FCSTD DOCUMENT  (FreeCAD 0.21R33771 (Git))
Label: Model_2
License: All rights reserved
LicenseURL: http://en.wikipedia.org/wiki/All_rights_reserved
objects: Sketcher::SketchObject×2, App::FeaturePython×2, Spreadsheet::Sheet×1, App::DocumentObjectGroupPython×1
note: 2 computed .brp shape members not serialized (recipe doc carries the construction recipe); baked Part::Feature solids carry a one-line shape summary decoded from their .brp

FEATURE [Spreadsheet::Sheet] Spreadsheet  label="Parametry"
  cells = A1='Parametry palca pacjenta, wartości proszę wpisywać w milimetrach; A3='Proszę wrowadzić średnicę palca pacjenta; B3='Średnica palca; C3(Srednica)=20; A4='Proszę wprowadzić długość palca pacjenta; B4='Długość palca; C4(Dlugosc)=80
FEATURE [Sketcher::SketchObject] Sketch  label="Model_cięcia"
  FullyConstrained = true
  expr: Constraints[100] = <<Parametry>>.Srednica / 2
  expr: Constraints[101] = <<Parametry>>.Srednica / 2
  expr: Constraints[102] = <<Parametry>>.Srednica / 2
  expr: Constraints[137] = <<Parametry>>.Dlugosc + 10
  expr: Constraints[15] = <<Parametry>>.Srednica / 2
  expr: Constraints[16] = <<Parametry>>.Srednica / 2
  expr: Constraints[17] = <<Parametry>>.Srednica / 2
  expr: Constraints[18] = <<Parametry>>.Srednica / 2
  expr: Constraints[19] = <<Parametry>>.Srednica / 2
  expr: Constraints[20] = <<Parametry>>.Srednica / 2
  expr: Constraints[21] = <<Parametry>>.Srednica / 2
  expr: Constraints[22] = <<Parametry>>.Srednica / 2
  expr: Constraints[31] = <<Parametry>>.Srednica / 2
  expr: Constraints[32] = <<Parametry>>.Srednica / 2
  expr: Constraints[33] = <<Parametry>>.Srednica / 2
  expr: Constraints[34] = <<Parametry>>.Srednica / 2
  expr: Constraints[35] = <<Parametry>>.Srednica / 2
  expr: Constraints[36] = <<Parametry>>.Srednica / 2
  expr: Constraints[37] = <<Parametry>>.Srednica / 2
  expr: Constraints[38] = <<Parametry>>.Srednica / 2
  expr: Constraints[79] = <<Parametry>>.Srednica / 2
  expr: Constraints[80] = <<Parametry>>.Srednica / 2
  expr: Constraints[81] = <<Parametry>>.Srednica / 2
  expr: Constraints[82] = <<Parametry>>.Srednica / 2
  expr: Constraints[83] = <<Parametry>>.Srednica / 2
  expr: Constraints[84] = <<Parametry>>.Srednica / 2
  expr: Constraints[85] = <<Parametry>>.Srednica / 2
  expr: Constraints[86] = <<Parametry>>.Srednica / 2
  expr: Constraints[95] = <<Parametry>>.Srednica / 2
  expr: Constraints[96] = <<Parametry>>.Srednica / 2
  expr: Constraints[97] = <<Parametry>>.Srednica / 2
  expr: Constraints[98] = <<Parametry>>.Srednica / 2
  expr: Constraints[99] = <<Parametry>>.Srednica / 2
  sketch-geometry (56):
    g0: LineSegment StartX=0 StartY=0 StartZ=0 EndX=90 EndY=0 EndZ=0
    g1: LineSegment StartX=90 StartY=0 StartZ=0 EndX=90 EndY=60 EndZ=0
    g2: LineSegment StartX=90 StartY=60 StartZ=0 EndX=0 EndY=60 EndZ=0
    g3: LineSegment StartX=0 StartY=60 StartZ=0 EndX=0 EndY=0 EndZ=0
    g4: GeomPoint X=15 Y=15 Z=0
    g5: LineSegment StartX=15 StartY=5 StartZ=0 EndX=15 EndY=25 EndZ=0
    g6: LineSegment StartX=5 StartY=15 StartZ=0 EndX=25 EndY=15 EndZ=0
    g7: LineSegment StartX=7.92893 StartY=22.0711 StartZ=0 EndX=22.0711 EndY=7.92893 EndZ=0
    g8: LineSegment StartX=7.92893 StartY=7.92893 StartZ=0 EndX=22.0711 EndY=22.0711 EndZ=0
    g9: GeomPoint X=15 Y=45 Z=0
    g10: LineSegment StartX=15 StartY=35 StartZ=0 EndX=15 EndY=55 EndZ=0
    g11: LineSegment StartX=5 StartY=45 StartZ=0 EndX=25 EndY=45 EndZ=0
    g12: LineSegment StartX=7.92893 StartY=52.0711 StartZ=0 EndX=22.0711 EndY=37.9289 EndZ=0
    g13: LineSegment StartX=7.92893 StartY=37.9289 StartZ=0 EndX=22.0711 EndY=52.0711 EndZ=0
    g14: Circle CenterX=7.92893 CenterY=52.0711 CenterZ=0 NormalX=0 NormalY=0 NormalZ=1 AngleXU=0 Radius=0.25
    g15: Circle CenterX=15 CenterY=55 CenterZ=0 NormalX=0 NormalY=0 NormalZ=1 AngleXU=0 Radius=0.25
    g16: Circle CenterX=22.0711 CenterY=52.0711 CenterZ=0 NormalX=0 NormalY=0 NormalZ=1 AngleXU=0 Radius=0.25
    g17: Circle CenterX=25 CenterY=45 CenterZ=0 NormalX=0 NormalY=0 NormalZ=1 AngleXU=0 Radius=0.25
    g18: Circle CenterX=22.0711 CenterY=37.9289 CenterZ=0 NormalX=0 NormalY=0 NormalZ=1 AngleXU=0 Radius=0.25
    g19: Circle CenterX=15 CenterY=35 CenterZ=0 NormalX=0 NormalY=0 NormalZ=1 AngleXU=0 Radius=0.25
    g20: Circle CenterX=7.92893 CenterY=37.9289 CenterZ=0 NormalX=0 NormalY=0 NormalZ=1 AngleXU=0 Radius=0.25
    g21: Circle CenterX=5 CenterY=45 CenterZ=0 NormalX=0 NormalY=0 NormalZ=1 AngleXU=0 Radius=0.25
    g22: Circle CenterX=5 CenterY=15 CenterZ=0 NormalX=0 NormalY=0 NormalZ=1 AngleXU=0 Radius=0.25
    g23: Circle CenterX=7.92893 CenterY=22.0711 CenterZ=0 NormalX=0 NormalY=0 NormalZ=1 AngleXU=0 Radius=0.25
    g24: Circle CenterX=15 CenterY=25 CenterZ=0 NormalX=0 NormalY=0 NormalZ=1 AngleXU=0 Radius=0.25
    g25: Circle CenterX=22.0711 CenterY=22.0711 CenterZ=0 NormalX=0 NormalY=0 NormalZ=1 AngleXU=0 Radius=0.25
    g26: Circle CenterX=25 CenterY=15 CenterZ=0 NormalX=0 NormalY=0 NormalZ=1 AngleXU=0 Radius=0.25
    g27: Circle CenterX=22.0711 CenterY=7.92893 CenterZ=0 NormalX=0 NormalY=0 NormalZ=1 AngleXU=0 Radius=0.25
    g28: Circle CenterX=15 CenterY=5 CenterZ=0 NormalX=0 NormalY=0 NormalZ=1 AngleXU=0 Radius=0.25
    g29: Circle CenterX=7.92893 CenterY=7.92893 CenterZ=0 NormalX=0 NormalY=0 NormalZ=1 AngleXU=0 Radius=0.25
    g30: GeomPoint X=75 Y=15 Z=0
    g31: LineSegment StartX=75 StartY=5 StartZ=0 EndX=75 EndY=25 EndZ=0
    g32: LineSegment StartX=65 StartY=15 StartZ=0 EndX=85 EndY=15 EndZ=0
    g33: LineSegment StartX=67.9289 StartY=22.0711 StartZ=0 EndX=82.0711 EndY=7.92893 EndZ=0
    g34: LineSegment StartX=67.9289 StartY=7.92893 StartZ=0 EndX=82.0711 EndY=22.0711 EndZ=0
    g35: GeomPoint X=75 Y=45 Z=0
    g36: LineSegment StartX=75 StartY=35 StartZ=0 EndX=75 EndY=55 EndZ=0
    g37: LineSegment StartX=65 StartY=45 StartZ=0 EndX=85 EndY=45 EndZ=0
    g38: LineSegment StartX=67.9289 StartY=52.0711 StartZ=0 EndX=82.0711 EndY=37.9289 EndZ=0
    g39: LineSegment StartX=67.9289 StartY=37.9289 StartZ=0 EndX=82.0711 EndY=52.0711 EndZ=0
    g40: Circle CenterX=67.9289 CenterY=52.0711 CenterZ=0 NormalX=0 NormalY=0 NormalZ=1 AngleXU=0 Radius=0.25
    g41: Circle CenterX=75 CenterY=55 CenterZ=0 NormalX=0 NormalY=0 NormalZ=1 AngleXU=0 Radius=0.25
    g42: Circle CenterX=82.0711 CenterY=52.0711 CenterZ=0 NormalX=0 NormalY=0 NormalZ=1 AngleXU=0 Radius=0.25
    g43: Circle CenterX=85 CenterY=45 CenterZ=0 NormalX=0 NormalY=0 NormalZ=1 AngleXU=0 Radius=0.25
    g44: Circle CenterX=82.0711 CenterY=37.9289 CenterZ=0 NormalX=0 NormalY=0 NormalZ=1 AngleXU=0 Radius=0.25
    g45: Circle CenterX=75 CenterY=35 CenterZ=0 NormalX=0 NormalY=0 NormalZ=1 AngleXU=0 Radius=0.25
    g46: Circle CenterX=67.9289 CenterY=37.9289 CenterZ=0 NormalX=0 NormalY=0 NormalZ=1 AngleXU=0 Radius=0.25
    g47: Circle CenterX=65 CenterY=45 CenterZ=0 NormalX=0 NormalY=0 NormalZ=1 AngleXU=0 Radius=0.25
    g48: Circle CenterX=65 CenterY=15 CenterZ=0 NormalX=0 NormalY=0 NormalZ=1 AngleXU=0 Radius=0.25
    g49: Circle CenterX=67.9289 CenterY=22.0711 CenterZ=0 NormalX=0 NormalY=0 NormalZ=1 AngleXU=0 Radius=0.25
    g50: Circle CenterX=75 CenterY=25 CenterZ=0 NormalX=0 NormalY=0 NormalZ=1 AngleXU=0 Radius=0.25
    g51: Circle CenterX=82.0711 CenterY=22.0711 CenterZ=0 NormalX=0 NormalY=0 NormalZ=1 AngleXU=0 Radius=0.25
    g52: Circle CenterX=85 CenterY=15 CenterZ=0 NormalX=0 NormalY=0 NormalZ=1 AngleXU=0 Radius=0.25
    g53: Circle CenterX=82.0711 CenterY=7.92893 CenterZ=0 NormalX=0 NormalY=0 NormalZ=1 AngleXU=0 Radius=0.25
    g54: Circle CenterX=75 CenterY=5 CenterZ=0 NormalX=0 NormalY=0 NormalZ=1 AngleXU=0 Radius=0.25
    g55: Circle CenterX=67.9289 CenterY=7.92893 CenterZ=0 NormalX=0 NormalY=0 NormalZ=1 AngleXU=0 Radius=0.25
  constraints (147):
    c: Coincident(g0,g1)
    c: Coincident(g1,g2)
    c: Coincident(g2,g3)
    c: Coincident(g3,g0)
    c: Horizontal(g0)
    c: Horizontal(g2)
    c: Vertical(g1)
    c: Vertical(g3)
    c: Coincident(g0,g-1)
    c: Vertical(g5)
    c: Horizontal(g6)
    c: PointOnObject(g4,g7)
    c: PointOnObject(g4,g5)
    c: PointOnObject(g4,g6)
    c: PointOnObject(g4,g8)
    c: Distance(g6,g4) = 10
    c: Distance(g7,g4) = 10
    c: Distance(g5,g4) = 10
    c: Distance(g8,g4) = 10
    c: Distance(g6,g4) = 10
    c: Distance(g7,g4) = 10
    c: Distance(g5,g4) = 10
    c: Distance(g4,g8) = 10
    c: Angle(g6,g8) = 0.785398
    c: Angle(g7,g6) = 0.785398
    c: Vertical(g10)
    c: Horizontal(g11)
    c: PointOnObject(g9,g12)
    c: PointOnObject(g9,g10)
    c: PointOnObject(g9,g11)
    c: PointOnObject(g9,g13)
    c: Distance(g11,g9) = 10
    c: Distance(g12,g9) = 10
    c: Distance(g10,g9) = 10
    c: Distance(g13,g9) = 10
    c: Distance(g11,g9) = 10
    c: Distance(g12,g9) = 10
    c: Distance(g10,g9) = 10
    c: Distance(g9,g13) = 10
    c: Angle(g11,g13) = 0.785398
    c: Angle(g12,g11) = 0.785398
    c: Coincident(g14,g12)
    c: Coincident(g15,g10)
    c: Coincident(g16,g13)
    c: Coincident(g17,g11)
    c: Coincident(g18,g12)
    c: Coincident(g19,g10)
    c: Coincident(g20,g13)
    c: Coincident(g21,g11)
    c: Coincident(g22,g6)
    c: Coincident(g23,g7)
    c: Coincident(g24,g5)
    c: Coincident(g25,g8)
    c: Coincident(g26,g6)
    c: Coincident(g27,g7)
    c: Coincident(g28,g5)
    c: Coincident(g29,g8)
    c: Diameter(g26) = 0.5
    c: Diameter(g27) = 0.5
    c: Diameter(g28) = 0.5
    c: Diameter(g29) = 0.5
    c: Diameter(g22) = 0.5
    c: Diameter(g23) = 0.5
    c: Diameter(g24) = 0.5
    c: Diameter(g25) = 0.5
    c: Diameter(g19) = 0.5
    c: Diameter(g20) = 0.5
    c: Diameter(g21) = 0.5
    c: Diameter(g18) = 0.5
    c: Diameter(g17) = 0.5
    c: Diameter(g16) = 0.5
    c: Diameter(g15) = 0.5
    c: Diameter(g14) = 0.5
    c: Vertical(g31)
    c: Horizontal(g32)
    c: PointOnObject(g30,g33)
    c: PointOnObject(g30,g31)
    c: PointOnObject(g30,g32)
    c: PointOnObject(g30,g34)
    c: Distance(g32,g30) = 10
    c: Distance(g33,g30) = 10
    c: Distance(g31,g30) = 10
    c: Distance(g34,g30) = 10
    c: Distance(g32,g30) = 10
    c: Distance(g33,g30) = 10
    c: Distance(g31,g30) = 10
    c: Distance(g30,g34) = 10
    c: Angle(g32,g34) = 0.785398
    c: Angle(g33,g32) = 0.785398
    c: Vertical(g36)
    c: Horizontal(g37)
    c: PointOnObject(g35,g38)
    c: PointOnObject(g35,g36)
    c: PointOnObject(g35,g37)
    c: PointOnObject(g35,g39)
    c: Distance(g37,g35) = 10
    c: Distance(g38,g35) = 10
    c: Distance(g36,g35) = 10
    c: Distance(g39,g35) = 10
    c: Distance(g37,g35) = 10
    c: Distance(g38,g35) = 10
    c: Distance(g36,g35) = 10
    c: Distance(g35,g39) = 10
    c: Angle(g37,g39) = 0.785398
    c: Angle(g38,g37) = 0.785398
    c: Coincident(g40,g38)
    c: Coincident(g41,g36)
    c: Coincident(g42,g39)
    c: Coincident(g43,g37)
    c: Coincident(g44,g38)
    c: Coincident(g45,g36)
    c: Coincident(g46,g39)
    c: Coincident(g47,g37)
    c: Coincident(g48,g32)
    c: Coincident(g49,g33)
    c: Coincident(g50,g31)
    c: Coincident(g51,g34)
    c: Coincident(g52,g32)
    c: Coincident(g53,g33)
    c: Coincident(g54,g31)
    c: Coincident(g55,g34)
    c: Equal(g26,g52) = 0.5
    c: Equal(g27,g53) = 0.5
    c: Equal(g28,g54) = 0.5
    c: Equal(g29,g55) = 0.5
    c: Equal(g22,g48) = 0.5
    c: Equal(g23,g49) = 0.5
    c: Equal(g24,g50) = 0.5
    c: Equal(g25,g51) = 0.5
    c: Equal(g19,g45) = 0.5
    c: Equal(g20,g46) = 0.5
    c: Equal(g21,g47) = 0.5
    c: Equal(g18,g44) = 0.5
    c: Equal(g17,g43) = 0.5
    c: Equal(g16,g42) = 0.5
    c: Equal(g15,g41) = 0.5
    c: Equal(g14,g40) = 0.5
    c: DistanceX(g0,g0) = 90
    c: DistanceY(g0,g5) = 5
    c: DistanceY(g0,g31) = 5
    c: DistanceY(g10,g2) = 5
    c: DistanceY(g36,g1) = 5
    c: DistanceX(g0,g6) = 5
    c: DistanceX(g32,g0) = 5
    c: DistanceX(g2,g11) = 5
    c: DistanceX(g37,g1) = 5
    c: DistanceY(g31,g36) = 10
FEATURE [App::FeaturePython] Layer  label="Cięcie laserem"  # WARN: FeaturePython — macro-defined, semantics opaque (R4)
  Group = -> [Sketch]
FEATURE [Sketcher::SketchObject] Sketch001  label="Model_zgrzewania"
  FullyConstrained = true
  expr: Constraints[10] = <<Parametry>>.Srednica / 2 + 5
  expr: Constraints[11] = <<Parametry>>.Srednica / 2 + 5
  expr: Constraints[12] = <<Parametry>>.Srednica / 2 + 5
  expr: Constraints[13] = <<Parametry>>.Srednica / 2 + 3
  expr: Constraints[14] = <<Parametry>>.Dlugosc + 10 - 2
  expr: Constraints[5] = <<Parametry>>.Srednica + 3
  expr: Constraints[6] = <<Parametry>>.Srednica + 3
  expr: Constraints[9] = <<Parametry>>.Srednica + 10
  sketch-geometry (5):
    g0: LineSegment StartX=88 StartY=30 StartZ=0 EndX=88 EndY=2 EndZ=0
    g1: LineSegment StartX=88 StartY=2 StartZ=0 EndX=2 EndY=2 EndZ=0
    g2: LineSegment StartX=2 StartY=2 StartZ=0 EndX=2 EndY=30 EndZ=0
    g3: Circle CenterX=15 CenterY=15 CenterZ=0 NormalX=0 NormalY=0 NormalZ=1 AngleXU=0 Radius=11.5
    g4: Circle CenterX=75 CenterY=15 CenterZ=0 NormalX=0 NormalY=0 NormalZ=1 AngleXU=0 Radius=11.5
  constraints (16):
    c: Coincident(g0,g1)
    c: Coincident(g1,g2)
    c: Horizontal(g1)
    c: Vertical(g0)
    c: Vertical(g2)
    c: Diameter(g3) = 23
    c: Diameter(g4) = 23
    c: DistanceX(g-1,g1) = 2
    c: DistanceY(g-1,g1) = 2
    c: DistanceY(g-1,g2) = 30
    c: DistanceY(g-1,g3) = 15
    c: DistanceY(g-1,g4) = 15
    c: DistanceX(g-1,g3) = 15
    c: DistanceX(g4,g0) = 13
    c: DistanceX(g-1,g0) = 88
    c: Equal(g0,g2)
FEATURE [App::FeaturePython] Layer001  label="Zgrzewanie"  # WARN: FeaturePython — macro-defined, semantics opaque (R4)
  Group = -> [Sketch001]
FEATURE [App::DocumentObjectGroupPython] LayerContainer  label="Warstwy"  # scripted group (container) (typed FeaturePython)
  Group = -> [Layer,Layer001]
